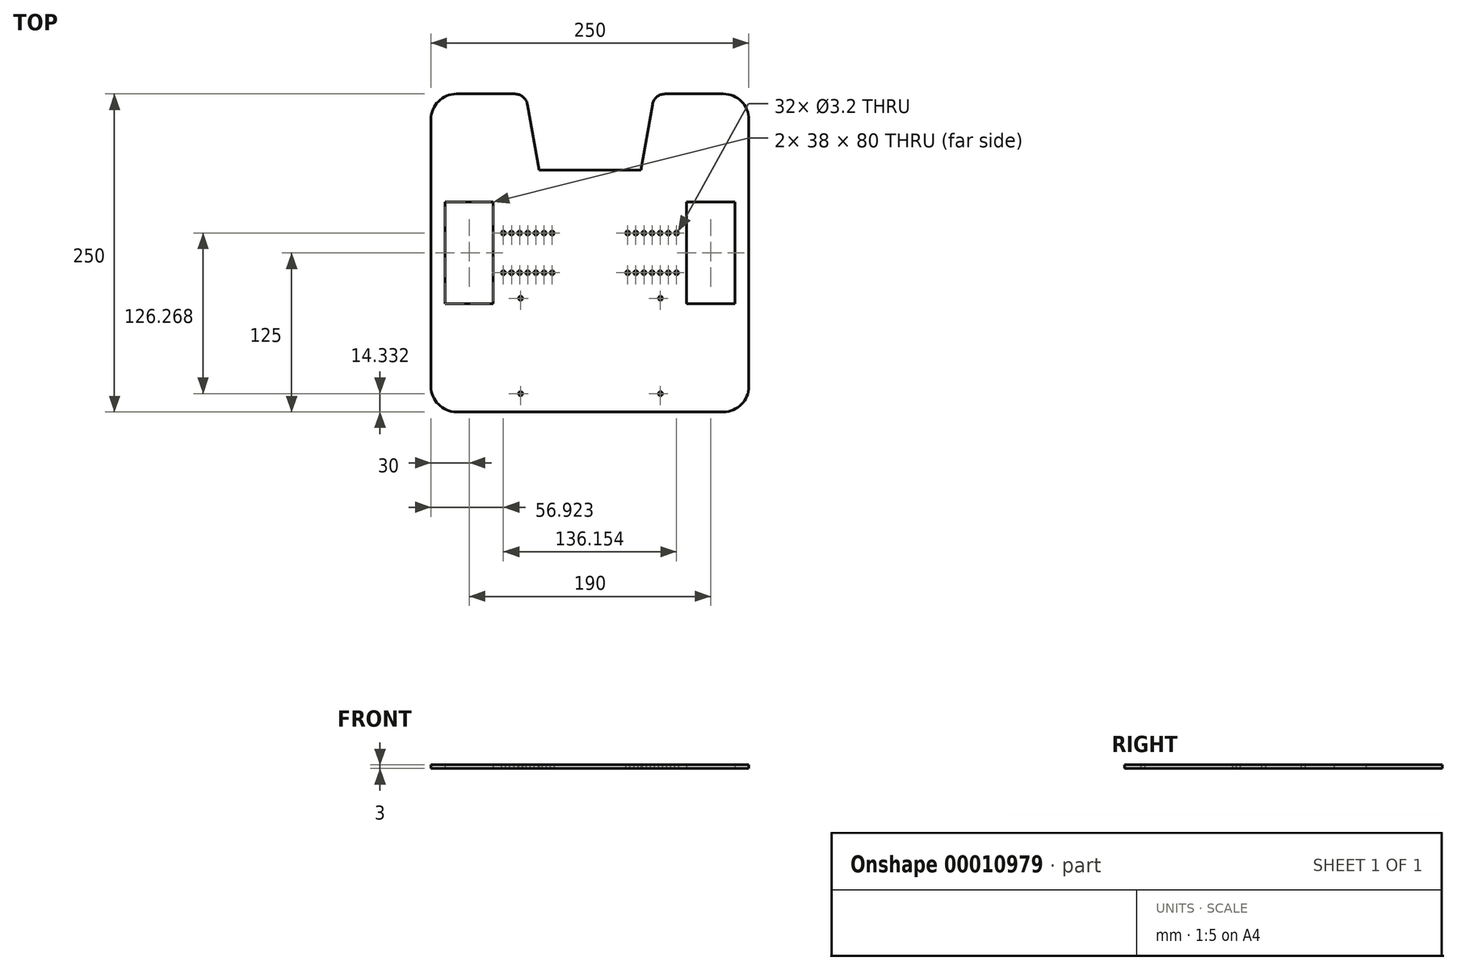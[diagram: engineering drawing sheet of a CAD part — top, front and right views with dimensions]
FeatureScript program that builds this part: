
annotation { "Feature Type Name" : "Feature", "Feature Type Description" : "" }
export const myFeature = defineFeature(function(context is Context, id is Id, definition is map)
    precondition{}
    {
        {
            var Q0;
            Q0=qCreatedBy(makeId("Top.planeOp"),FACE);
            var sketch = newSketch(context, id + "F0", { "sketchPlane" : qUnion([Q0])});
            skLineSegment(sketch, "E0.rect.bottom", {"start": v(105, -125) * mm, "end": v(-105, -125) * mm});
            skLineSegment(sketch, "E0.rect.left", {"start": v(125, -105) * mm, "end": v(125, 105) * mm});
            skLineSegment(sketch, "E0.rect.right", {"start": v(-125, -105) * mm, "end": v(-125, 105) * mm});
            skPoint(sketch, "E0.rect.middle", {"position": v(0, 0) * mm});
            skLineSegment(sketch, "E1.direction2", {"start": v(-68.08, 15.6) * mm, "end": v(-68.08, -15.6) * mm, "construction": true});
            skLineSegment(sketch, "E1.direction1", {"start": v(-68.08, 15.6) * mm, "end": v(-61.68, 15.6) * mm, "construction": true});
            skCircle(sketch, "E1.1.0.0", {"center": v(-61.68, 15.6) * mm, "radius": 1.6 * mm});
            skCircle(sketch, "E1.0.1.0", {"center": v(-68.08, -15.6) * mm, "radius": 1.6 * mm});
            skCircle(sketch, "E1.2.0.0", {"center": v(-55.28, 15.6) * mm, "radius": 1.6 * mm});
            skCircle(sketch, "E1.1.1.0", {"center": v(-61.68, -15.6) * mm, "radius": 1.6 * mm});
            skCircle(sketch, "E1.3.0.0", {"center": v(-48.88, 15.6) * mm, "radius": 1.6 * mm});
            skCircle(sketch, "E1.2.1.0", {"center": v(-55.28, -15.6) * mm, "radius": 1.6 * mm});
            skCircle(sketch, "E1.4.0.0", {"center": v(-42.48, 15.6) * mm, "radius": 1.6 * mm});
            skCircle(sketch, "E1.6.1.0", {"center": v(-29.68, -15.6) * mm, "radius": 1.6 * mm});
            skCircle(sketch, "E1.3.1.0", {"center": v(-48.88, -15.6) * mm, "radius": 1.6 * mm});
            skCircle(sketch, "E1.5.0.0", {"center": v(-36.08, 15.6) * mm, "radius": 1.6 * mm});
            skCircle(sketch, "E1.5.1.0", {"center": v(-36.08, -15.6) * mm, "radius": 1.6 * mm});
            skCircle(sketch, "E1.4.1.0", {"center": v(-42.48, -15.6) * mm, "radius": 1.6 * mm});
            skCircle(sketch, "E2", {"center": v(-68.08, 15.6) * mm, "radius": 1.6 * mm});
            skCircle(sketch, "E1.6.0.0", {"center": v(-29.68, 15.6) * mm, "radius": 1.6 * mm});
            skLineSegment(sketch, "E3.direction1", {"start": v(29.68, 15.6) * mm, "end": v(36.08, 15.6) * mm, "construction": true});
            skLineSegment(sketch, "E3.direction2", {"start": v(29.68, 15.6) * mm, "end": v(29.68, -15.6) * mm, "construction": true});
            skCircle(sketch, "E3.5.0.0", {"center": v(61.68, 15.6) * mm, "radius": 1.6 * mm});
            skCircle(sketch, "E3.6.1.0", {"center": v(68.08, -15.6) * mm, "radius": 1.6 * mm});
            skCircle(sketch, "E3.3.1.0", {"center": v(48.88, -15.6) * mm, "radius": 1.6 * mm});
            skCircle(sketch, "E3.6.0.0", {"center": v(68.08, 15.6) * mm, "radius": 1.6 * mm});
            skCircle(sketch, "E3.2.1.0", {"center": v(42.48, -15.6) * mm, "radius": 1.6 * mm});
            skCircle(sketch, "E3.4.1.0", {"center": v(55.28, -15.6) * mm, "radius": 1.6 * mm});
            skCircle(sketch, "E3.4.0.0", {"center": v(55.28, 15.6) * mm, "radius": 1.6 * mm});
            skCircle(sketch, "E3.1.1.0", {"center": v(36.08, -15.6) * mm, "radius": 1.6 * mm});
            skCircle(sketch, "E3.3.0.0", {"center": v(48.88, 15.6) * mm, "radius": 1.6 * mm});
            skCircle(sketch, "E3.0.1.0", {"center": v(29.68, -15.6) * mm, "radius": 1.6 * mm});
            skCircle(sketch, "E3.2.0.0", {"center": v(42.48, 15.6) * mm, "radius": 1.6 * mm});
            skCircle(sketch, "E3.1.0.0", {"center": v(36.08, 15.6) * mm, "radius": 1.6 * mm});
            skCircle(sketch, "E3.5.1.0", {"center": v(61.68, -15.6) * mm, "radius": 1.6 * mm});
            skCircle(sketch, "E4", {"center": v(29.68, 15.6) * mm, "radius": 1.6 * mm});
            skLineSegment(sketch, "E5.rect.bottom", {"start": v(-76, -40) * mm, "end": v(-114, -40) * mm});
            skLineSegment(sketch, "E5.rect.top", {"start": v(-76, 40) * mm, "end": v(-114, 40) * mm});
            skLineSegment(sketch, "E5.rect.left", {"start": v(-76, -40) * mm, "end": v(-76, 40) * mm});
            skLineSegment(sketch, "E5.rect.right", {"start": v(-114, -40) * mm, "end": v(-114, 40) * mm});
            skPoint(sketch, "E5.rect.middle", {"position": v(-95, 0) * mm});
            skLineSegment(sketch, "E6.rect.bottom", {"start": v(114, -40) * mm, "end": v(76, -40) * mm});
            skLineSegment(sketch, "E6.rect.top", {"start": v(114, 40) * mm, "end": v(76, 40) * mm});
            skLineSegment(sketch, "E6.rect.left", {"start": v(114, -40) * mm, "end": v(114, 40) * mm});
            skLineSegment(sketch, "E6.rect.right", {"start": v(76, -40) * mm, "end": v(76, 40) * mm});
            skPoint(sketch, "E6.rect.middle", {"position": v(95, 0) * mm});
            skLineSegment(sketch, "E7.top", {"start": v(-40, 65) * mm, "end": v(40, 65) * mm});
            skLineSegment(sketch, "E7.left", {"start": v(-49.12, 116.74) * mm, "end": v(-40, 65) * mm});
            skLineSegment(sketch, "E7.right", {"start": v(49.12, 116.74) * mm, "end": v(40, 65) * mm});
            skLineSegment(sketch, "E8", {"start": v(-105, 125) * mm, "end": v(-58.97, 125) * mm});
            skLineSegment(sketch, "E9", {"start": v(58.97, 125) * mm, "end": v(105, 125) * mm});
            skPoint(sketch, "E10.visualSharp", {"position": v(-125, 125) * mm});
            skArc(sketch, "E10.filletArc", {"start": v(-105, 125) * mm, "mid": v(-119.14, 119.14) * mm, "end": v(-125, 105) * mm});
            skPoint(sketch, "E11.visualSharp", {"position": v(125, 125) * mm});
            skArc(sketch, "E11.filletArc", {"start": v(125, 105) * mm, "mid": v(119.14, 119.14) * mm, "end": v(105, 125) * mm});
            skPoint(sketch, "E12.visualSharp", {"position": v(125, -125) * mm});
            skArc(sketch, "E12.filletArc", {"start": v(105, -125) * mm, "mid": v(119.14, -119.14) * mm, "end": v(125, -105) * mm});
            skPoint(sketch, "E13.visualSharp", {"position": v(-125, -125) * mm});
            skArc(sketch, "E13.filletArc", {"start": v(-125, -105) * mm, "mid": v(-119.14, -119.14) * mm, "end": v(-105, -125) * mm});
            skPoint(sketch, "E14.visualSharp", {"position": v(-50.58, 125) * mm});
            skArc(sketch, "E14.filletArc", {"start": v(-49.12, 116.74) * mm, "mid": v(-52.54, 122.66) * mm, "end": v(-58.97, 125) * mm});
            skPoint(sketch, "E15.visualSharp", {"position": v(50.58, 125) * mm});
            skArc(sketch, "E15.filletArc", {"start": v(58.97, 125) * mm, "mid": v(52.54, 122.66) * mm, "end": v(49.12, 116.74) * mm});
            skPoint(sketch, "E16", {"position": v(0, 65) * mm});
            skLineSegment(sketch, "E17.direction2", {"start": v(-54.54, -35.67) * mm, "end": v(-54.54, -110.67) * mm, "construction": true});
            skLineSegment(sketch, "E17.direction1", {"start": v(-54.54, -35.67) * mm, "end": v(55.46, -35.67) * mm, "construction": true});
            skPoint(sketch, "E18.rect.middle", {"position": v(9.2, -69.54) * mm});
            skCircle(sketch, "E17.1.0.0", {"center": v(55.46, -35.67) * mm, "radius": 1.6 * mm});
            skCircle(sketch, "E17.1.1.0", {"center": v(55.46, -110.67) * mm, "radius": 1.6 * mm});
            skCircle(sketch, "E17.0.1.0", {"center": v(-54.54, -110.67) * mm, "radius": 1.6 * mm});
            skCircle(sketch, "E19", {"center": v(-54.54, -35.67) * mm, "radius": 1.6 * mm});
            skSolve(sketch);
        }
        {
            var Q0;
            Q0 = qSketchRegion(id + "F0", true);
            extrude(context, id + "F1", {"entities" : qUnion([Q0]), "depth" : 3 * mm});
        }
    });
